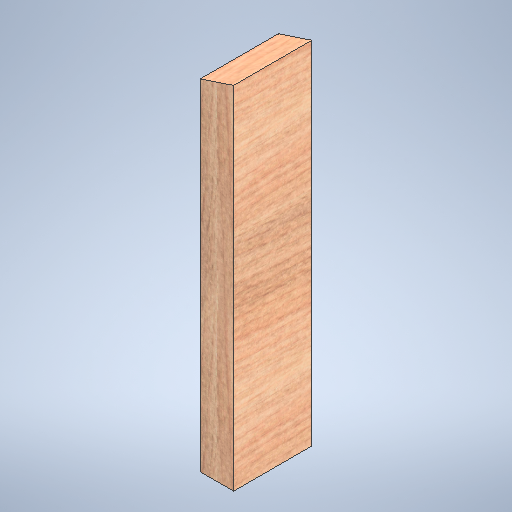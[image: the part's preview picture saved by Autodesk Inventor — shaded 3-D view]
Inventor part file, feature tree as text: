
AUTODESK INVENTOR PART (.ipt)
format: ipt  version: 2025.1 (Build 291241020, 241B)  size: 381,440 bytes
history: native  units: in
note: dims shown in document units (in); Inventor stores cm internally (conversion verified against a paired STEP export)
features: extrude x1, sketch x1
ambient origin geometry x8: Origin, YZ Plane, XZ Plane, XY Plane, X Axis, Y Axis, Z Axis, Center Point
bodies: Solid1 (feature_tree)
feature tree (2):
  extrude  "Extrusion1"  Depth=3.5in TaperAngle=0.0deg
  sketch  "Sketch1"  dims[d2=1.5in d3=3.5in d4=0.0in d5=15.224in d6=15.724in]
